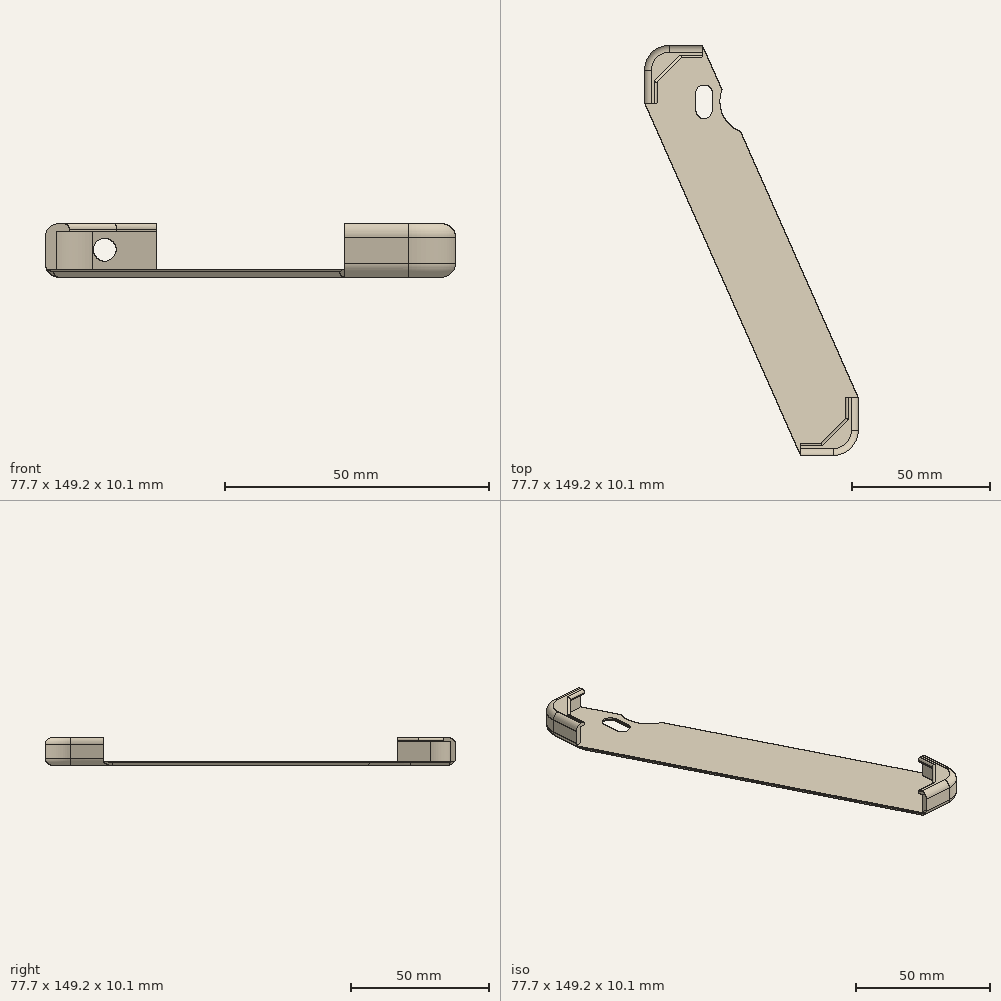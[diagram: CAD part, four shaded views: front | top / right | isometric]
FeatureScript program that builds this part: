
annotation { "Feature Type Name" : "Feature", "Feature Type Description" : "" }
export const myFeature = defineFeature(function(context is Context, id is Id, definition is map)
    precondition{}
    {
        {
            var Q0;
            Q0=qCreatedBy(makeId("Top.planeOp"),FACE);
            var sketch = newSketch(context, id + "F0", { "sketchPlane" : qUnion([Q0])});
            skLineSegment(sketch, "E0.bottom", {"start": v(29.85, 72.6) * mm, "end": v(-29.85, 72.6) * mm, "construction": true});
            skLineSegment(sketch, "E0.top", {"start": v(29.85, -72.6) * mm, "end": v(-29.85, -72.6) * mm, "construction": true});
            skLineSegment(sketch, "E0.left", {"start": v(36.85, 65.6) * mm, "end": v(36.85, -65.6) * mm, "construction": true});
            skLineSegment(sketch, "E0.right", {"start": v(-36.85, 65.6) * mm, "end": v(-36.85, -65.6) * mm, "construction": true});
            skPoint(sketch, "E0.middle", {"position": v(0, 0) * mm});
            skPoint(sketch, "E1.visualSharp", {"position": v(36.85, 72.6) * mm});
            skArc(sketch, "E1.filletArc", {"start": v(36.85, 65.6) * mm, "mid": v(34.8, 70.55) * mm, "end": v(29.85, 72.6) * mm, "construction": true});
            skPoint(sketch, "E2.visualSharp", {"position": v(-36.85, 72.6) * mm});
            skArc(sketch, "E2.filletArc", {"start": v(-29.85, 72.6) * mm, "mid": v(-34.8, 70.55) * mm, "end": v(-36.85, 65.6) * mm, "construction": true});
            skPoint(sketch, "E3.visualSharp", {"position": v(-36.85, -72.6) * mm});
            skArc(sketch, "E3.filletArc", {"start": v(-36.85, -65.6) * mm, "mid": v(-34.8, -70.55) * mm, "end": v(-29.85, -72.6) * mm, "construction": true});
            skPoint(sketch, "E4.visualSharp", {"position": v(36.85, -72.6) * mm});
            skArc(sketch, "E4.filletArc", {"start": v(29.85, -72.6) * mm, "mid": v(34.8, -70.55) * mm, "end": v(36.85, -65.6) * mm, "construction": true});
            skCircle(sketch, "E5", {"center": v(0, 54.1) * mm, "radius": 11.5 * mm, "construction": true});
            skLineSegment(sketch, "E6.bottom", {"start": v(17.25, 47.98) * mm, "end": v(17.25, 47.98) * mm});
            skLineSegment(sketch, "E6.top", {"start": v(17.25, 60.23) * mm, "end": v(17.25, 60.23) * mm});
            skLineSegment(sketch, "E6.left", {"start": v(20.25, 50.97) * mm, "end": v(20.25, 57.23) * mm, "construction": true});
            skLineSegment(sketch, "E6.right", {"start": v(14.25, 50.97) * mm, "end": v(14.25, 57.23) * mm, "construction": true});
            skPoint(sketch, "E6.middle", {"position": v(17.25, 54.1) * mm});
            skArc(sketch, "E7", {"start": v(20.25, 57.23) * mm, "mid": v(17.25, 60.23) * mm, "end": v(14.25, 57.23) * mm, "construction": true});
            skPoint(sketch, "E7.first.point", {"position": v(14.25, 57.23) * mm});
            skPoint(sketch, "E7.second.point", {"position": v(17.25, 60.23) * mm});
            skPoint(sketch, "E7.third.point", {"position": v(20.25, 57.23) * mm});
            skArc(sketch, "E8", {"start": v(14.25, 50.97) * mm, "mid": v(17.25, 47.97) * mm, "end": v(20.25, 50.97) * mm, "construction": true});
            skPoint(sketch, "E8.first.point", {"position": v(20.25, 50.97) * mm});
            skPoint(sketch, "E8.second.point", {"position": v(17.25, 47.98) * mm});
            skPoint(sketch, "E8.third.point", {"position": v(14.25, 50.97) * mm});
            skPoint(sketch, "E9.orphan", {"position": v(14.25, 60.23) * mm});
            skPoint(sketch, "E10.orphan", {"position": v(20.25, 60.23) * mm});
            skPoint(sketch, "E11.orphan", {"position": v(20.25, 47.98) * mm});
            skPoint(sketch, "E12.orphan", {"position": v(14.25, 47.98) * mm});
            skArc(sketch, "E13.MirrorCS", {"start": v(-14.25, 50.97) * mm, "mid": v(-17.25, 47.97) * mm, "end": v(-20.25, 50.97) * mm, "construction": true});
            skLineSegment(sketch, "E14.MirrorCS", {"start": v(-20.25, 50.97) * mm, "end": v(-20.25, 57.23) * mm, "construction": true});
            skLineSegment(sketch, "E15.MirrorCS", {"start": v(-14.25, 50.97) * mm, "end": v(-14.25, 57.23) * mm, "construction": true});
            skArc(sketch, "E16.MirrorCS", {"start": v(-20.25, 57.23) * mm, "mid": v(-17.25, 60.23) * mm, "end": v(-14.25, 57.23) * mm, "construction": true});
            skSolve(sketch);
        }
        {
            var Q0;
            Q0=qCreatedBy(makeId("Top.planeOp"),FACE);
            var sketch = newSketch(context, id + "F1", { "sketchPlane" : qUnion([Q0])});
            skArc(sketch, "E17.0", {"start": v(-29.85, 74.6) * mm, "mid": v(-36.21, 71.96) * mm, "end": v(-38.85, 65.6) * mm});
            skArc(sketch, "E18.0", {"start": v(29.85, -74.6) * mm, "mid": v(36.21, -71.96) * mm, "end": v(38.85, -65.6) * mm});
            skLineSegment(sketch, "E19", {"start": v(38.85, -65.6) * mm, "end": v(38.85, -53.6) * mm});
            skLineSegment(sketch, "E20", {"start": v(29.85, -74.6) * mm, "end": v(17.85, -74.6) * mm});
            skLineSegment(sketch, "E21", {"start": v(-29.85, 74.6) * mm, "end": v(-17.85, 74.6) * mm});
            skLineSegment(sketch, "E22", {"start": v(-38.85, 65.6) * mm, "end": v(-38.85, 53.6) * mm});
            skLineSegment(sketch, "E23", {"start": v(-17.85, 74.6) * mm, "end": v(-10.68, 58.38) * mm});
            skLineSegment(sketch, "E24", {"start": v(-38.85, 53.6) * mm, "end": v(17.85, -74.6) * mm});
            skArc(sketch, "E25.0", {"start": v(-10.68, 58.38) * mm, "mid": v(-10.52, 49.45) * mm, "end": v(-4.02, 43.32) * mm});
            skArc(sketch, "E26.0", {"start": v(-20.25, 57.23) * mm, "mid": v(-17.25, 60.23) * mm, "end": v(-14.25, 57.23) * mm});
            skPoint(sketch, "E27.0", {"position": v(-14.25, 54.1) * mm});
            skLineSegment(sketch, "E28.0", {"start": v(-14.25, 50.97) * mm, "end": v(-14.25, 57.23) * mm});
            skArc(sketch, "E29.0", {"start": v(-14.25, 50.97) * mm, "mid": v(-17.25, 47.97) * mm, "end": v(-20.25, 50.97) * mm});
            skLineSegment(sketch, "E30.0", {"start": v(-20.25, 50.97) * mm, "end": v(-20.25, 57.23) * mm});
            skLineSegment(sketch, "E31.trimOffspring", {"start": v(-4.02, 43.32) * mm, "end": v(38.85, -53.6) * mm});
            skSolve(sketch);
        }
        {
            var Q0;
            Q0=makeQuery(id+"F1.imprint","IMPRINT",FACE,{"disambiguationData":[TD([[makeQuery(id+"F1.imprint","IMPRINT",EDGE,{"derivedFrom":sQuery(id+"F1.wireOp",EDGE,"E17.0")}),1.0]])]});
            extrude(context, id + "F2", {"entities" : qUnion([Q0]), "oppositeDirection" : true, "depth" : 1.5 * mm, "offsetDistance" : 25 * mm});
        }
        {
            var Q0;
            Q0=qCreatedBy(makeId("Top.planeOp"),FACE);
            var sketch = newSketch(context, id + "F3", { "sketchPlane" : qUnion([Q0])});
            skArc(sketch, "E32.0", {"start": v(-29.85, 72.6) * mm, "mid": v(-34.8, 70.55) * mm, "end": v(-36.85, 65.6) * mm});
            skLineSegment(sketch, "E33.0", {"start": v(-17.85, 72.6) * mm, "end": v(-29.85, 72.6) * mm});
            skLineSegment(sketch, "E34.0", {"start": v(-36.85, 65.6) * mm, "end": v(-36.85, 53.6) * mm});
            skLineSegment(sketch, "E35.0", {"start": v(36.85, -53.6) * mm, "end": v(36.85, -65.6) * mm});
            skArc(sketch, "E36.0", {"start": v(29.85, -72.6) * mm, "mid": v(34.8, -70.55) * mm, "end": v(36.85, -65.6) * mm});
            skLineSegment(sketch, "E37.0", {"start": v(29.85, -72.6) * mm, "end": v(17.85, -72.6) * mm});
            skLineSegment(sketch, "E38.0", {"start": v(38.85, -65.6) * mm, "end": v(38.85, -53.6) * mm});
            skArc(sketch, "E39.0", {"start": v(29.85, -74.6) * mm, "mid": v(36.21, -71.96) * mm, "end": v(38.85, -65.6) * mm});
            skLineSegment(sketch, "E40.0", {"start": v(29.85, -74.6) * mm, "end": v(17.85, -74.6) * mm});
            skLineSegment(sketch, "E41.0", {"start": v(-38.85, 65.6) * mm, "end": v(-38.85, 53.6) * mm});
            skArc(sketch, "E42.0", {"start": v(-29.85, 74.6) * mm, "mid": v(-36.21, 71.96) * mm, "end": v(-38.85, 65.6) * mm});
            skLineSegment(sketch, "E43.0", {"start": v(-29.85, 74.6) * mm, "end": v(-17.85, 74.6) * mm});
            skLineSegment(sketch, "E44", {"start": v(-17.85, 74.6) * mm, "end": v(-17.85, 72.6) * mm});
            skLineSegment(sketch, "E45", {"start": v(-38.85, 53.6) * mm, "end": v(-36.85, 53.6) * mm});
            skLineSegment(sketch, "E46", {"start": v(38.85, -53.6) * mm, "end": v(36.85, -53.6) * mm});
            skLineSegment(sketch, "E47", {"start": v(17.85, -74.6) * mm, "end": v(17.85, -72.6) * mm});
            skPoint(sketch, "E48.orphan", {"position": v(-29.85, -72.6) * mm});
            skPoint(sketch, "E49.orphan", {"position": v(-36.85, -65.6) * mm});
            skPoint(sketch, "E50.orphan", {"position": v(36.85, 65.6) * mm});
            skPoint(sketch, "E51.orphan", {"position": v(29.85, 72.6) * mm});
            skSolve(sketch);
        }
        {
            var Q0;
            Q0=makeQuery(id+"F3.imprint","IMPRINT",FACE,{"disambiguationData":[TD([[makeQuery(id+"F3.imprint","IMPRINT",EDGE,{"derivedFrom":sQuery(id+"F3.wireOp",EDGE,"E32.0")}),-1.0]])]});
            var Q1;
            Q1=makeQuery(id+"F3.imprint","IMPRINT",FACE,{"disambiguationData":[TD([[makeQuery(id+"F3.imprint","IMPRINT",EDGE,{"derivedFrom":sQuery(id+"F3.wireOp",EDGE,"E35.0")}),1.0]])]});
            extrude(context, id + "F4", {"entities" : qUnion([Q0, Q1]), "operationType" : NewBodyOperationType.ADD, "depth" : 7.1 * mm, "offsetDistance" : 25 * mm});
        }
        {
            var Q0;
            Q0=makeQuery(id+"F4.opExtrude","CAP_FACE",FACE,{"disambiguationData":[OSD([sQuery(id+"F3.wireOp",EDGE,"E32.0"),sQuery(id+"F3.wireOp",EDGE,"E33.0"),sQuery(id+"F3.wireOp",EDGE,"E34.0"),sQuery(id+"F3.wireOp",EDGE,"E41.0"),sQuery(id+"F3.wireOp",EDGE,"E42.0"),sQuery(id+"F3.wireOp",EDGE,"E43.0"),sQuery(id+"F3.wireOp",EDGE,"E44"),sQuery(id+"F3.wireOp",EDGE,"E45")])],"isStart":false});
            var sketch = newSketch(context, id + "F5", { "sketchPlane" : qUnion([Q0])});
            skArc(sketch, "E52.0", {"start": v(-29.85, 70.1) * mm, "mid": v(-33.03, 68.78) * mm, "end": v(-34.35, 65.6) * mm});
            skArc(sketch, "E53.0", {"start": v(29.85, -70.1) * mm, "mid": v(33.03, -68.78) * mm, "end": v(34.35, -65.6) * mm});
            skLineSegment(sketch, "E54", {"start": v(34.35, -65.6) * mm, "end": v(34.35, -53.6) * mm});
            skLineSegment(sketch, "E55", {"start": v(29.85, -70.1) * mm, "end": v(17.85, -70.1) * mm});
            skLineSegment(sketch, "E56.0", {"start": v(-29.85, 74.6) * mm, "end": v(-17.85, 74.6) * mm});
            skArc(sketch, "E57.0", {"start": v(-29.85, 74.6) * mm, "mid": v(-36.21, 71.96) * mm, "end": v(-38.85, 65.6) * mm});
            skLineSegment(sketch, "E58.0", {"start": v(-38.85, 65.6) * mm, "end": v(-38.85, 53.6) * mm});
            skLineSegment(sketch, "E59.0", {"start": v(38.85, -65.6) * mm, "end": v(38.85, -53.6) * mm});
            skArc(sketch, "E60.0", {"start": v(29.85, -74.6) * mm, "mid": v(36.21, -71.96) * mm, "end": v(38.85, -65.6) * mm});
            skLineSegment(sketch, "E61.0", {"start": v(29.85, -74.6) * mm, "end": v(17.85, -74.6) * mm});
            skLineSegment(sketch, "E62", {"start": v(-29.85, 70.1) * mm, "end": v(-17.85, 70.1) * mm});
            skLineSegment(sketch, "E63", {"start": v(-17.85, 70.1) * mm, "end": v(-17.85, 74.6) * mm});
            skLineSegment(sketch, "E64", {"start": v(-34.35, 65.6) * mm, "end": v(-34.35, 53.6) * mm});
            skLineSegment(sketch, "E65", {"start": v(-34.35, 53.6) * mm, "end": v(-38.85, 53.6) * mm});
            skLineSegment(sketch, "E66", {"start": v(38.85, -53.6) * mm, "end": v(34.35, -53.6) * mm});
            skLineSegment(sketch, "E67", {"start": v(17.85, -74.6) * mm, "end": v(17.85, -70.1) * mm});
            skLineSegment(sketch, "E68", {"start": v(34.35, -61.1) * mm, "end": v(25.35, -70.1) * mm});
            skLineSegment(sketch, "E69", {"start": v(-34.35, 61.1) * mm, "end": v(-25.35, 70.1) * mm});
            skSolve(sketch);
        }
        {
            var Q0;
            {var subQ2=sQuery(id+"F5.wireOp",EDGE,"E56.0");Q0=makeQuery(id+"F5.imprint","IMPRINT",FACE,{"disambiguationData":[TD([[makeQuery(id+"F5.imprint","IMPRINT",EDGE,{"derivedFrom":subQ2}),-1.0]])]});}
            var Q1;
            Q1=makeQuery(id+"F5.imprint","IMPRINT",FACE,{"disambiguationData":[TD([[makeQuery(id+"F5.imprint","IMPRINT",EDGE,{"derivedFrom":sQuery(id+"F5.wireOp",EDGE,"E52.0")}),-1.0]])]});
            var Q2;
            Q2=makeQuery(id+"F5.imprint","IMPRINT",FACE,{"disambiguationData":[TD([[makeQuery(id+"F5.imprint","IMPRINT",EDGE,{"derivedFrom":sQuery(id+"F5.wireOp",EDGE,"E53.0")}),-1.0]])]});
            var Q3;
            {var subQ0=sQuery(id+"F5.wireOp",EDGE,"E53.0");Q3=makeQuery(id+"F5.imprint","IMPRINT",FACE,{"disambiguationData":[TD([[makeQuery(id+"F5.imprint","IMPRINT",EDGE,{"derivedFrom":subQ0}),1.0]])]});}
            var Q4;
            {var subQ0=sQuery(id+"F5.wireOp",EDGE,"E52.0");Q4=makeQuery(id+"F5.imprint","IMPRINT",FACE,{"disambiguationData":[TD([[makeQuery(id+"F5.imprint","IMPRINT",EDGE,{"derivedFrom":subQ0}),1.0]])]});}
            extrude(context, id + "F6", {"entities" : qUnion([Q0, Q1, Q2, Q3, Q4]), "operationType" : NewBodyOperationType.ADD, "depth" : 1.5 * mm, "offsetDistance" : 25 * mm});
        }
        {
            var Q0;
            Q0=makeQuery(id+"F6.boolean.opBoolean","MERGE",FACE,{"derivedFrom":[makeQuery(id+"F4.boolean.opBoolean","MERGE",FACE,{"derivedFrom":[makeQuery(id+"F2.opExtrude","SWEPT_FACE",FACE,{"disambiguationData":[OSD([sQuery(id+"F1.wireOp",EDGE,"E21")])]}),makeQuery(id+"F4.opExtrude","SWEPT_FACE",FACE,{"disambiguationData":[OSD([sQuery(id+"F3.wireOp",EDGE,"E43.0")])]})]}),makeQuery(id+"F6.opExtrude","SWEPT_FACE",FACE,{"disambiguationData":[OSD([sQuery(id+"F5.wireOp",EDGE,"E56.0")])]})]});
            var sketch = newSketch(context, id + "F7", { "sketchPlane" : qUnion([Q0])});
            skCircle(sketch, "E70", {"center": v(27.6, 3.67) * mm, "radius": 2.15 * mm});
            skSolve(sketch);
        }
        {
            var Q0;
            Q0=makeQuery(id+"F7.imprint","IMPRINT",FACE,{"disambiguationData":[TD([[makeQuery(id+"F7.imprint","IMPRINT",EDGE,{"derivedFrom":sQuery(id+"F7.wireOp",EDGE,"E70")}),1.0]])]});
            extrude(context, id + "F8", {"entities" : qUnion([Q0]), "operationType" : NewBodyOperationType.REMOVE, "oppositeDirection" : true, "depth" : 25 * mm, "offsetDistance" : 25 * mm});
        }
        {
            var Q0;
            Q0=makeQuery(id+"F6.opExtrude","CAP_EDGE",EDGE,{"disambiguationData":[OSD([sQuery(id+"F5.wireOp",EDGE,"E59.0")])],"isStart":false});
            var Q1;
            Q1=makeQuery(id+"F2.opExtrude","CAP_EDGE",EDGE,{"disambiguationData":[OSD([sQuery(id+"F1.wireOp",EDGE,"E20")])],"isStart":false});
            var Q2;
            Q2=makeQuery(id+"F6.opExtrude","CAP_EDGE",EDGE,{"disambiguationData":[OSD([sQuery(id+"F5.wireOp",EDGE,"E57.0")])],"isStart":false});
            var Q3;
            Q3=makeQuery(id+"F2.opExtrude","CAP_EDGE",EDGE,{"disambiguationData":[OSD([sQuery(id+"F1.wireOp",EDGE,"E17.0")])],"isStart":false});
            fillet(context, id + "F9", {"entities" : qUnion([Q0, Q1, Q2, Q3]), "tangentPropagation" : true, "radius" : 2.5 * mm, "defaultsChanged" : true, "vertexSettings" : [], "allowEdgeOverflow" : false});
        }
        {
            var Q0;
            Q0=makeQuery(id+"F6.opExtrude","CAP_EDGE",EDGE,{"disambiguationData":[OSD([sQuery(id+"F5.wireOp",EDGE,"E62")])],"isStart":false});
            var Q1;
            Q1=makeQuery(id+"F6.opExtrude","CAP_EDGE",EDGE,{"disambiguationData":[OSD([sQuery(id+"F5.wireOp",EDGE,"E69")])],"isStart":false});
            var Q2;
            Q2=makeQuery(id+"F6.opExtrude","CAP_EDGE",EDGE,{"disambiguationData":[OSD([sQuery(id+"F5.wireOp",EDGE,"E64")])],"isStart":false});
            var Q3;
            Q3=makeQuery(id+"F6.opExtrude","CAP_EDGE",EDGE,{"disambiguationData":[OSD([sQuery(id+"F5.wireOp",EDGE,"E54")])],"isStart":false});
            var Q4;
            Q4=makeQuery(id+"F6.opExtrude","CAP_EDGE",EDGE,{"disambiguationData":[OSD([sQuery(id+"F5.wireOp",EDGE,"E68")])],"isStart":false});
            var Q5;
            Q5=makeQuery(id+"F6.opExtrude","CAP_EDGE",EDGE,{"disambiguationData":[OSD([sQuery(id+"F5.wireOp",EDGE,"E55")])],"isStart":false});
            var Q6;
            Q6=makeQuery(id+"F2.opExtrude","CAP_EDGE",EDGE,{"disambiguationData":[OSD([sQuery(id+"F1.wireOp",EDGE,"E31.trimOffspring")])],"isStart":false});
            var Q7;
            Q7=makeQuery(id+"F2.opExtrude","CAP_EDGE",EDGE,{"disambiguationData":[OSD([sQuery(id+"F1.wireOp",EDGE,"E23")])],"isStart":false});
            var Q8;
            Q8=makeQuery(id+"F2.opExtrude","CAP_EDGE",EDGE,{"disambiguationData":[OSD([sQuery(id+"F1.wireOp",EDGE,"E25.0")])],"isStart":false});
            var Q9;
            Q9=makeQuery(id+"F2.opExtrude","CAP_EDGE",EDGE,{"disambiguationData":[OSD([sQuery(id+"F1.wireOp",EDGE,"E29.0")])],"isStart":false});
            var Q10;
            Q10=makeQuery(id+"F2.opExtrude","CAP_EDGE",EDGE,{"disambiguationData":[OSD([sQuery(id+"F1.wireOp",EDGE,"E24")])],"isStart":false});
            fillet(context, id + "F10", {"entities" : qUnion([Q0, Q1, Q2, Q3, Q4, Q5, Q6, Q7, Q8, Q9, Q10]), "tangentPropagation" : true, "radius" : 1 * mm, "defaultsChanged" : false, "vertexSettings" : [], "allowEdgeOverflow" : false});
        }
    });
